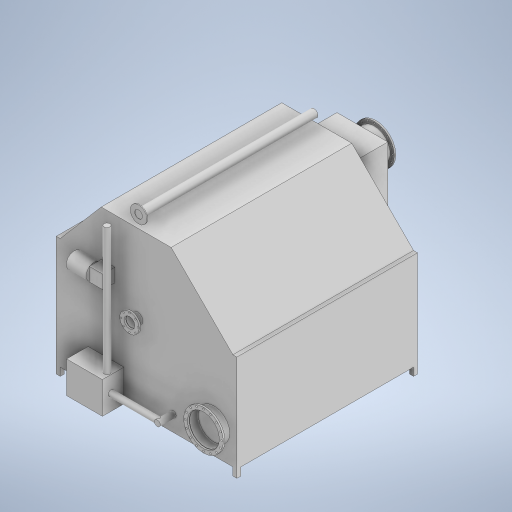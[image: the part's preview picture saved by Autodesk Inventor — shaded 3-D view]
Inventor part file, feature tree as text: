
AUTODESK INVENTOR PART (.ipt)
format: ipt  version: 2023.1 (Build 271208000, 208)  size: 625,664 bytes
history: native  units: mm
features: extrude x23, sketch x23, projected_geometry x16
ambient origin geometry x8: Origin, YZ Plane, XZ Plane, XY Plane, X Axis, Y Axis, Z Axis, Center Point
bodies: Solid1 (feature_tree)
feature tree (62):
  extrude  "Extrusion1"  Depth=100.0mm
  extrude  "Extrusion2"  Depth=1400.0mm
  extrude  "Extrusion3"  Depth=50.0mm
  extrude  "Extrusion4"  Depth=50.0mm
  extrude  "Extrusion5"  Depth=1100.327658mm
  extrude  "Extrusion6"  Depth=50.0mm
  extrude  "Extrusion7"  Depth=50.0mm TaperAngle=0.0deg
  extrude  "Extrusion8"  Depth=390.0mm
  extrude  "Extrusion9"  Depth=485.0mm
  extrude  "Extrusion10"  Depth=540.0mm
  extrude  "Extrusion11"  Depth=125.0mm
  extrude  "Extrusion12"  Depth=1312.5mm
  extrude  "Extrusion13"  Depth=80.0mm TaperAngle=0.0deg
  extrude  "Extrusion14"  Depth=460.0mm
  extrude  "Extrusion15"  Depth=160.0mm TaperAngle=360.0deg
  extrude  "Extrusion16"  Depth=245.0mm
  extrude  "Extrusion17"  Depth=18.0mm
  extrude  "Extrusion18"  Depth=80.0mm TaperAngle=0.0deg
  extrude  "Extrusion19"  Depth=170.0mm
  extrude  "Extrusion20"  Depth=1260.0mm
  extrude  "Extrusion21"  Depth=200.0mm
  extrude  "Extrusion22"  Depth=250.0mm TaperAngle=0.0deg
  extrude  "Extrusion23"  Depth=10.0mm
  sketch  "Sketch1"  dims[d0=2270.0mm d1=100.0mm]
  sketch  "Sketch2"  dims[d2=1220.0mm d3=1400.0mm]
  projected_geometry  "Projected Loop1"
  sketch  "Sketch3"  dims[d4=880.0mm d5=50.0mm]
  sketch  "Sketch4"  dims[d6=50.0mm d7=2000.0mm]
  projected_geometry  "Projected Loop2"
  sketch  "Sketch5"  dims[d8=790.0mm d9=1100.327658mm]
  sketch  "Sketch6"  dims[d10=2270.0mm d11=0.0mm d12=50.0mm]
  sketch  "Sketch7"  dims[d13=50.0mm d15=100.0mm d16=0.0mm]
  projected_geometry  "Projected Loop3"
  sketch  "Sketch8"  dims[d18=400.0mm d19=390.0mm]
  projected_geometry  "Projected Loop4"
  sketch  "Sketch9"  dims[d20=95.0mm d21=485.0mm]
  projected_geometry  "Projected Loop5"
  sketch  "Sketch10"  dims[d22=150.0mm d23=540.0mm]
  projected_geometry  "Projected Loop6"
  sketch  "Sketch11"  dims[d24=110.0mm d25=0.0mm d26=125.0mm]
  sketch  "Sketch12"  dims[d28=957.5mm d30=1312.5mm]
  projected_geometry  "Projected Loop7"
  sketch  "Sketch13"  dims[d31=5.0mm d32=80.0mm d33=0.0mm]
  projected_geometry  "Projected Loop8"
  sketch  "Sketch14"  dims[d34=500.0mm d35=460.0mm]
  projected_geometry  "Projected Loop9"
  sketch  "Sketch15"  dims[d36=22.0mm d37=160.0mm d39=360.0deg]
  projected_geometry  "Projected Loop10"
  sketch  "Sketch16"  dims[d41=20.0mm d42=0.0mm d43=245.0mm]
  projected_geometry  "Projected Loop11"
  sketch  "Sketch17"  dims[d44=210.0mm d45=18.0mm]
  projected_geometry  "Projected Loop12"
  sketch  "Sketch18"  dims[d46=80.0mm d48=360.0deg d50=20.0mm d51=0.0mm]
  sketch  "Sketch19"  dims[d52=170.0mm d53=170.0mm]
  sketch  "Sketch20"  dims[d54=1535.0mm d55=1260.0mm]
  projected_geometry  "Projected Loop13"
  sketch  "Sketch21"  dims[d56=150.0mm d57=0.0mm d58=200.0mm]
  projected_geometry  "Projected Loop14"
  sketch  "Sketch22"  dims[d59=90.0mm d60=250.0mm d61=0.0mm]
  projected_geometry  "Projected Loop15"
  sketch  "Sketch23"  dims[d62=400.0mm d63=400.0mm d64=450.0mm d65=270.0mm d66=0.0mm d67=75.0mm d68=200.0mm d69=800.0mm d70=200.0mm d71=0.0mm d72=100.0mm d73=75.0mm d74=2200.0mm d75=0.0mm d76=210.0mm d77=10.0mm d78=0.0mm d79=875.0mm d80=50.0mm d81=760.0mm d82=560.0mm d83=580.0mm d84=0.0mm d85=640.0mm d86=450.0mm d87=900.0mm d88=0.0mm d89=400.0mm d90=60.0mm d91=500.0mm d92=150.0mm d93=0.0mm d94=500.0mm d95=350.0mm d96=460.0mm d97=22.0mm d98=160.0mm d100=360.0deg d102=20.0mm d103=0.0mm d104=400.0mm d105=300.0mm d106=20.0mm d107=0.0mm d108=110.0mm d109=800.0mm d110=210.0mm d111=60.0mm d112=0.0mm d113=220.0mm d114=18.0mm d115=180.0mm d116=10.0mm d117=0.0mm d118=80.0mm d120=360.0deg d122=160.0mm d123=140.0mm d124=330.0mm d125=0.0mm d126=140.0mm d127=330.0mm d128=0.0mm d129=10.0mm d130=0.0mm d131=50.0mm d132=10.0mm d133=0.0mm d134=1020.0mm d135=1120.0mm]
  projected_geometry  "Projected Loop16"
